# Revit family: 35361USA_NEW
name_source: partatom
category: Plumbing Fixtures
revit_build: Autodesk Revit 2018 (Build: 20170223_1515(x64)
units: mm (PartAtom-declared; Revit-internal decimal feet)

## family parameters
Always vertical = No
Cut with Voids When Loaded = No
OmniClass Number = 23.45.00.00
OmniClass Title = Sanitary, Laundry, and Cleaning Equipment
Part Type = Normal
Room Calculation Point = No
Round Connector Dimension = Use Diameter
Shared = No
Work Plane-Based = No

## types (1)
- n.a.
    Always visible = Yes
    BIMobject category = Showers
    Design country = Germany
    EAN code = 4059625197318
    Edition number = 1
    IFC Classification = Sanitary Terminal
    Installation instructions = https://www.axor-design.com
    Manufacturer country = Germany
    Manufacturer name = AXOR
    Material 1 = AXOR - AXOR One - White
    Material 2 = AXOR - AXOR One - Brass
    Material 3 = AXOR - AXOR One - Green
    Material main = Chrome
    Product Guid = 850933dd-f985-4479-98fb-5d9458d1167d
    Product SKU = 35361USA
    Product data url = https://www.bimobject.com
    Product family = AXOR One
    Product group = Basic set shower
    Product name = 35361USA AXOR One Basic set for overhead shower 280 2jet with shower arm
    Product url = https://www.axor-design.com
    QR code = https://www.bimobject.com
    Technical description = https://www.axor-design.com
